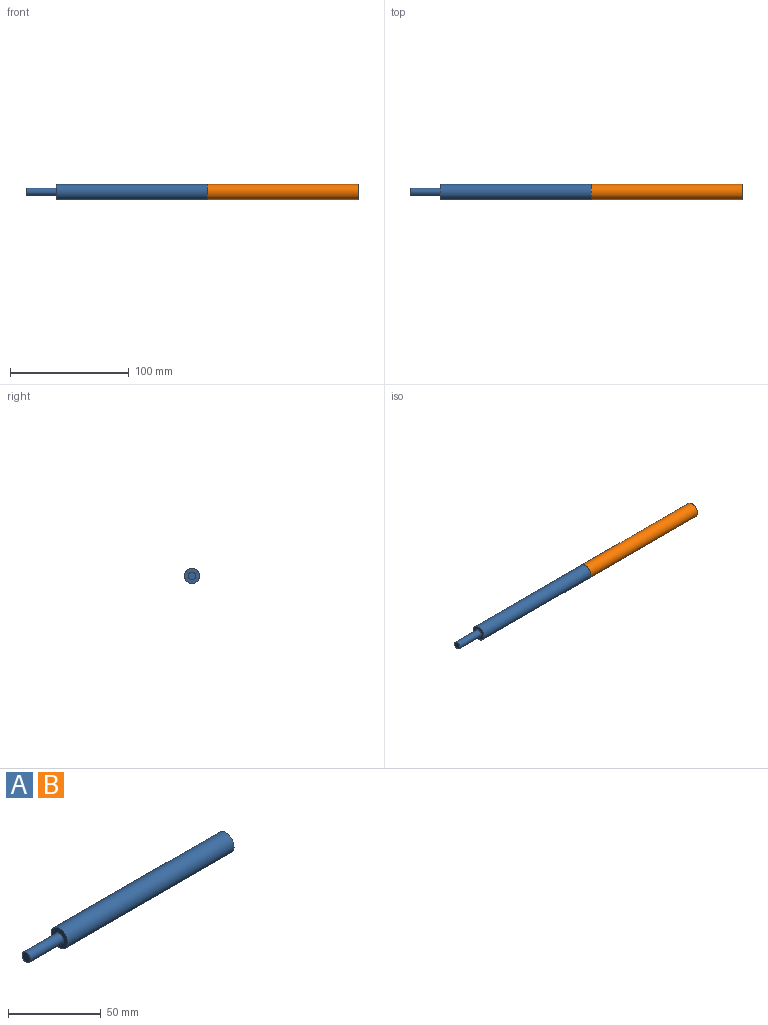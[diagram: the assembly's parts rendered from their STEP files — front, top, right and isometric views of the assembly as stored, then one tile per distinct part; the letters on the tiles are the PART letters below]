
ASSEMBLY  parts=2 mates=1
PART A: 7 faces, bbox 152.4x12.7x12.7 mm
  f0: plane 12.7x12.7mm, normal (-1,0,0), area 95mm2, adj f1,f4
  f1: cylinder r=3.17mm len=25.4mm, axis (-1,0,0), area 506.7mm2, adj f0,f2
  f2: plane 6.35x6.35mm, normal (-1,0,0), area 31.7mm2, adj f1
  f3: plane 12.7x12.7mm, normal (1,0,0), area 92.4mm2, adj f4,f6
  f4: cylinder r=6.35mm len=127mm, axis (-1,0,0), area 5067.1mm2, adj f0,f3
  f5: cone r=0mm half-angle=59deg, axis (1,0,0), area 40mm2, adj f6
  f6: cylinder r=3.3mm len=25.4mm, axis (1,0,0), area 527mm2, adj f3,f5
PART B: same geometry as A
PLACE A t=(-3.43,8.89,-32.07)mm
PLACE B t=(123.57,8.89,-32.07)mm
MATE pin_slot B.f1 <-> A.f1  axis (-1,0,0) through (50.54,-28.87,-32.07)mm
